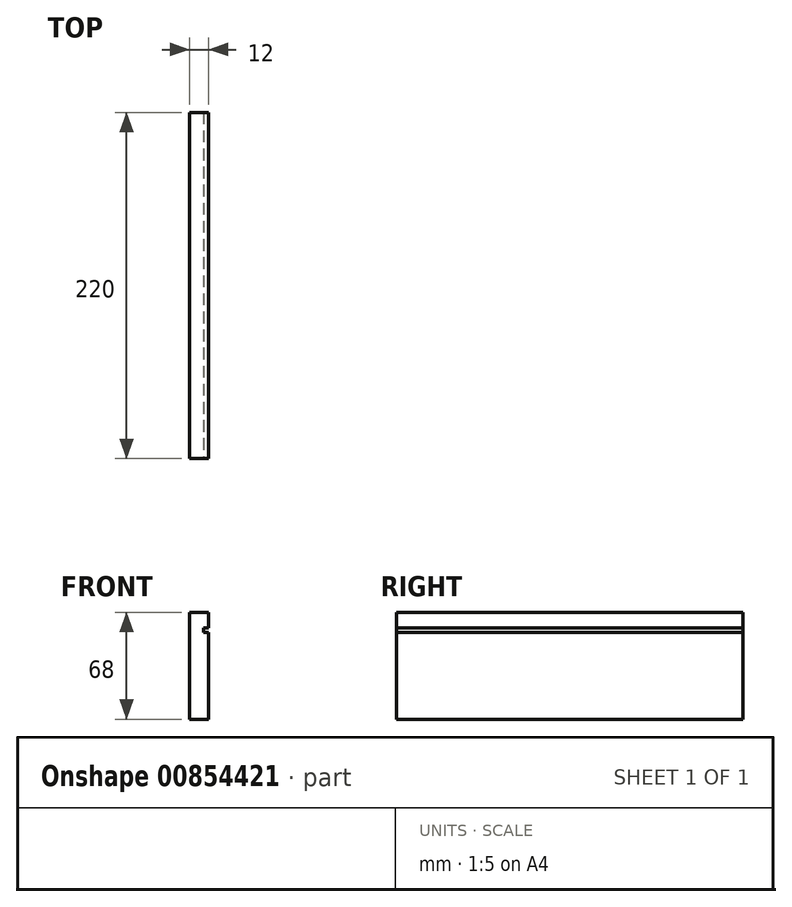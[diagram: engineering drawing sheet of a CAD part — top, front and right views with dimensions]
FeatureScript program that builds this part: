
annotation { "Feature Type Name" : "Feature", "Feature Type Description" : "" }
export const myFeature = defineFeature(function(context is Context, id is Id, definition is map)
    precondition{}
    {
        {
            var Q0;
            Q0=qCreatedBy(makeId("Front.planeOp"),FACE);
            var sketch = newSketch(context, id + "F0", { "sketchPlane" : qUnion([Q0])});
            skLineSegment(sketch, "E0.bottom", {"start": v(-110, 34) * mm, "end": v(110, 34) * mm});
            skLineSegment(sketch, "E0.top", {"start": v(-110, -34) * mm, "end": v(110, -34) * mm});
            skLineSegment(sketch, "E0.left", {"start": v(-110, 34) * mm, "end": v(-110, -34) * mm});
            skLineSegment(sketch, "E0.right", {"start": v(110, 34) * mm, "end": v(110, -34) * mm});
            skPoint(sketch, "E0.middle", {"position": v(0, 0) * mm});
            skSolve(sketch);
        }
        {
            var Q0;
            Q0 = qSketchRegion(id + "F0", true);
            extrude(context, id + "F1", {"entities" : qUnion([Q0]), "depth" : 12 * mm, "offsetDistance" : 25.4 * mm});
        }
        {
            var Q0;
            Q0=makeQuery(id+"F1.opExtrude","SWEPT_FACE",FACE,{"disambiguationData":[OSD([sQuery(id+"F0.wireOp",EDGE,"E0.right")])]});
            var sketch = newSketch(context, id + "F2", { "sketchPlane" : qUnion([Q0])});
            skLineSegment(sketch, "E1.bottom", {"start": v(0, 24) * mm, "end": v(-3, 24) * mm});
            skLineSegment(sketch, "E1.top", {"start": v(0, 21) * mm, "end": v(-3, 21) * mm});
            skLineSegment(sketch, "E1.left", {"start": v(0, 24) * mm, "end": v(0, 21) * mm});
            skLineSegment(sketch, "E1.right", {"start": v(-3, 24) * mm, "end": v(-3, 21) * mm});
            skSolve(sketch);
        }
        {
            var Q0;
            Q0 = qSketchRegion(id + "F2", true);
            extrude(context, id + "F3", {"entities" : qUnion([Q0]), "operationType" : NewBodyOperationType.REMOVE, "oppositeDirection" : true, "depth" : 300 * mm, "offsetDistance" : 25.4 * mm});
        }
        {
            var Q0;
            Q0=makeQuery(id+"F1.opExtrude","SWEPT_BODY",BODY,{"disambiguationData":[OSD([sQuery(id+"F0.wireOp",EDGE,"E0.bottom"),sQuery(id+"F0.wireOp",EDGE,"E0.top"),sQuery(id+"F0.wireOp",EDGE,"E0.left"),sQuery(id+"F0.wireOp",EDGE,"E0.right")])]});
            deleteBodies(context, id + "F4", {"entities" : qUnion([Q0])});
        }
        {
            var Q0;
            Q0=qCreatedBy(makeId("Front.planeOp"),FACE);
            var sketch = newSketch(context, id + "F5", { "sketchPlane" : qUnion([Q0])});
            skLineSegment(sketch, "E2.bottom", {"start": v(-6, 34) * mm, "end": v(6, 34) * mm});
            skLineSegment(sketch, "E2.top", {"start": v(-6, -34) * mm, "end": v(6, -34) * mm});
            skLineSegment(sketch, "E2.left", {"start": v(-6, 34) * mm, "end": v(-6, -34) * mm});
            skLineSegment(sketch, "E2.right", {"start": v(6, 34) * mm, "end": v(6, -34) * mm});
            skPoint(sketch, "E2.middle", {"position": v(0, 0) * mm});
            skSolve(sketch);
        }
        {
            var Q0;
            Q0=makeQuery(id+"F5.imprint","IMPRINT",FACE,{"disambiguationData":[TD([[makeQuery(id+"F5.imprint","IMPRINT",EDGE,{"derivedFrom":sQuery(id+"F5.wireOp",EDGE,"E2.bottom")}),-1.0]])]});
            extrude(context, id + "F6", {"entities" : qUnion([Q0]), "depth" : 220 * mm, "offsetDistance" : 25.4 * mm});
        }
        {
            var Q0;
            Q0=makeQuery(id+"F6.opExtrude","SWEPT_FACE",FACE,{"disambiguationData":[OSD([sQuery(id+"F5.wireOp",EDGE,"E2.right")])]});
            var sketch = newSketch(context, id + "F7", { "sketchPlane" : qUnion([Q0])});
            skLineSegment(sketch, "E3.bottom", {"start": v(0, 24) * mm, "end": v(-220, 24) * mm});
            skLineSegment(sketch, "E3.top", {"start": v(0, 21) * mm, "end": v(-220, 21) * mm});
            skLineSegment(sketch, "E3.left", {"start": v(0, 24) * mm, "end": v(0, 21) * mm});
            skLineSegment(sketch, "E3.right", {"start": v(-220, 24) * mm, "end": v(-220, 21) * mm});
            skSolve(sketch);
        }
        {
            var Q0;
            Q0 = qSketchRegion(id + "F7", true);
            extrude(context, id + "F8", {"entities" : qUnion([Q0]), "operationType" : NewBodyOperationType.REMOVE, "oppositeDirection" : true, "depth" : 3 * mm, "offsetDistance" : 25.4 * mm});
        }
    });
